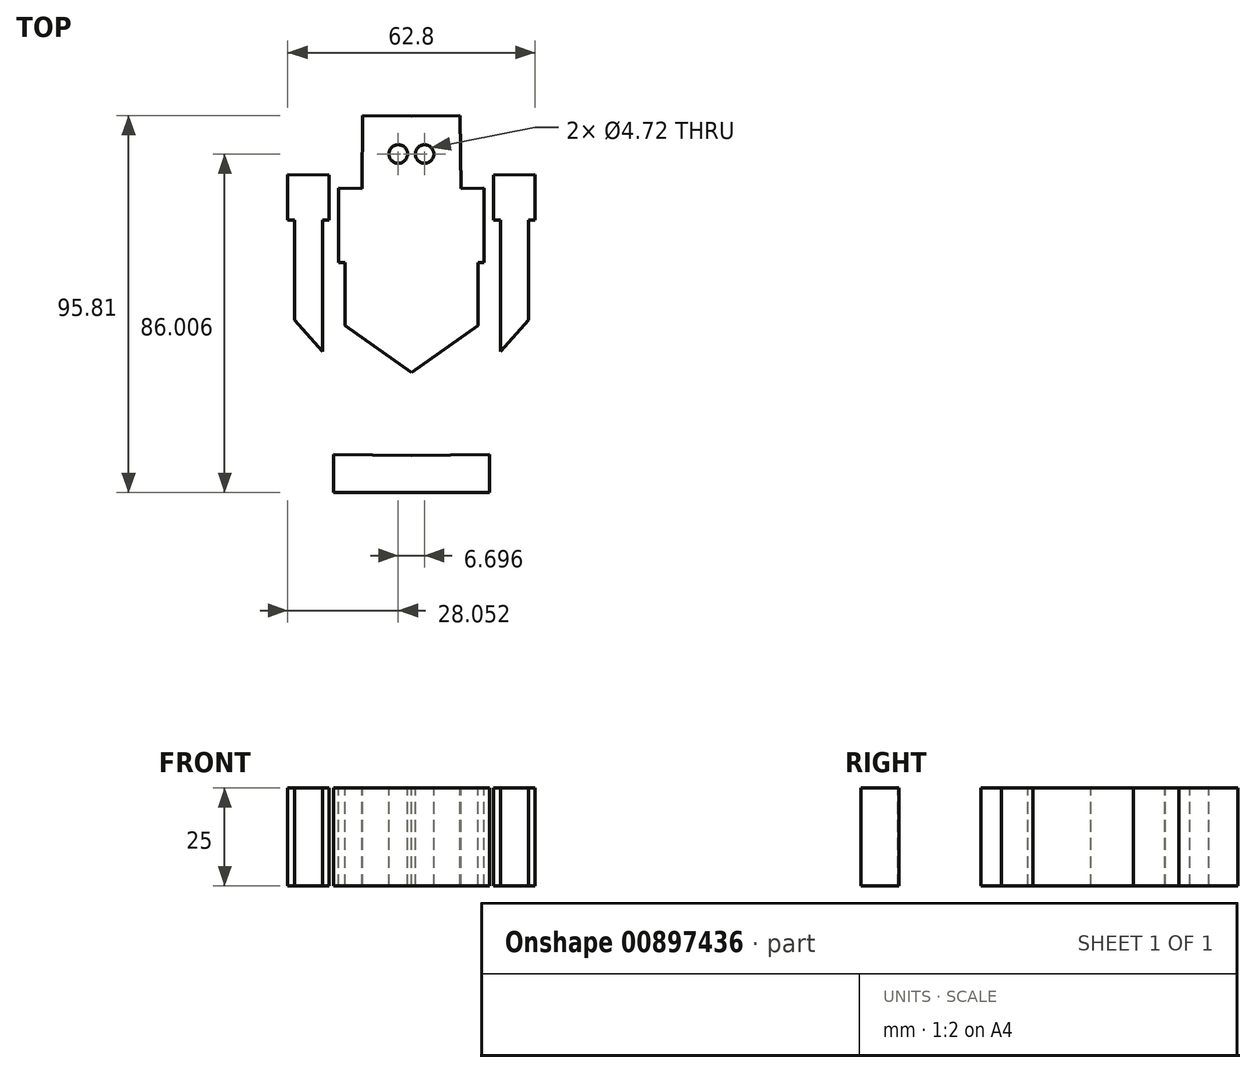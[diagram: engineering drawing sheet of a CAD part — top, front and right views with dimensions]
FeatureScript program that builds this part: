
annotation { "Feature Type Name" : "Feature", "Feature Type Description" : "" }
export const myFeature = defineFeature(function(context is Context, id is Id, definition is map)
    precondition{}
    {
        {
            var Q0;
            Q0=qCreatedBy(makeId("Top.planeOp"),FACE);
            var sketch = newSketch(context, id + "F0", { "sketchPlane" : qUnion([Q0])});
            skLineSegment(sketch, "E0", {"start": v(-49.7, 0) * mm, "end": v(50.3, 0) * mm});
            skLineSegment(sketch, "E1", {"start": v(0, 0) * mm, "end": v(0, 100) * mm});
            skSolve(sketch);
        }
        {
            var Q0;
            Q0=qCreatedBy(makeId("Top.planeOp"),FACE);
            var sketch = newSketch(context, id + "F1", { "sketchPlane" : qUnion([Q0])});
            skLineSegment(sketch, "E2", {"start": v(-31.4, 22.3) * mm, "end": v(-31.4, 10.7) * mm});
            skLineSegment(sketch, "E3", {"start": v(-31.4, 10.7) * mm, "end": v(-20.92, 10.7) * mm});
            skLineSegment(sketch, "E4", {"start": v(-20.92, 10.7) * mm, "end": v(-20.92, 22.18) * mm});
            skLineSegment(sketch, "E5", {"start": v(-20.92, 22.18) * mm, "end": v(-31.4, 22.3) * mm});
            skLineSegment(sketch, "E6", {"start": v(-29.73, 10.7) * mm, "end": v(-29.73, -14.7) * mm});
            skLineSegment(sketch, "E7", {"start": v(-29.73, -14.7) * mm, "end": v(-22.6, -14.78) * mm});
            skLineSegment(sketch, "E8", {"start": v(-22.6, -14.78) * mm, "end": v(-22.6, 10.7) * mm});
            skLineSegment(sketch, "E9", {"start": v(-22.6, -14.78) * mm, "end": v(-22.6, -22.7) * mm});
            skLineSegment(sketch, "E10", {"start": v(-22.6, -22.7) * mm, "end": v(-29.73, -14.7) * mm});
            skLineSegment(sketch, "E11", {"start": v(-19.8, -58.48) * mm, "end": v(-19.8, -48.82) * mm});
            skLineSegment(sketch, "E12", {"start": v(-19.8, -48.82) * mm, "end": v(0, -49.03) * mm});
            skLineSegment(sketch, "E13", {"start": v(-12.9, -48.9) * mm, "end": v(-12.59, -19.79) * mm});
            skLineSegment(sketch, "E14", {"start": v(0, -28.01) * mm, "end": v(-16.87, -16.08) * mm});
            skLineSegment(sketch, "E15", {"start": v(-16.87, -16.08) * mm, "end": v(-16.87, 0) * mm});
            skLineSegment(sketch, "E16", {"start": v(-16.87, -16.08) * mm, "end": v(0, -16.26) * mm});
            skLineSegment(sketch, "E17", {"start": v(0, 18.65) * mm, "end": v(-18.45, 18.84) * mm});
            skLineSegment(sketch, "E18", {"start": v(-18.45, 18.84) * mm, "end": v(-18.45, 0) * mm});
            skLineSegment(sketch, "E19", {"start": v(-18.45, 0) * mm, "end": v(0, 0) * mm});
            skLineSegment(sketch, "E20", {"start": v(0, 0) * mm, "end": v(0, 18.65) * mm});
            skLineSegment(sketch, "E21", {"start": v(-12.59, 18.65) * mm, "end": v(-12.4, 37.33) * mm});
            skLineSegment(sketch, "E22", {"start": v(-12.4, 37.33) * mm, "end": v(0, 37.2) * mm});
            skCircle(sketch, "E23", {"center": v(-3.35, 27.53) * mm, "radius": 2.36 * mm});
            skLineSegment(sketch, "E24.MirrorCS", {"start": v(12.4, 37.33) * mm, "end": v(0, 37.2) * mm});
            skLineSegment(sketch, "E25.MirrorCS", {"start": v(12.59, 18.65) * mm, "end": v(12.4, 37.33) * mm});
            skCircle(sketch, "E26.MirrorC", {"center": v(3.35, 27.53) * mm, "radius": 2.36 * mm});
            skLineSegment(sketch, "E27.MirrorCS", {"start": v(0, 18.65) * mm, "end": v(18.45, 18.84) * mm});
            skLineSegment(sketch, "E28.MirrorCS", {"start": v(18.45, 18.84) * mm, "end": v(18.45, 0) * mm});
            skLineSegment(sketch, "E29.MirrorCS", {"start": v(18.45, 0) * mm, "end": v(0, 0) * mm});
            skLineSegment(sketch, "E30.MirrorCS", {"start": v(16.87, -16.08) * mm, "end": v(16.87, 0) * mm});
            skLineSegment(sketch, "E31.MirrorCS", {"start": v(16.87, -16.08) * mm, "end": v(0, -16.26) * mm});
            skLineSegment(sketch, "E32.MirrorCS", {"start": v(0, -28.01) * mm, "end": v(16.87, -16.08) * mm});
            skLineSegment(sketch, "E33.MirrorCS", {"start": v(12.9, -48.9) * mm, "end": v(12.59, -19.79) * mm});
            skLineSegment(sketch, "E34.MirrorCS", {"start": v(19.8, -48.82) * mm, "end": v(0, -49.03) * mm});
            skLineSegment(sketch, "E35.MirrorCS", {"start": v(19.8, -58.48) * mm, "end": v(19.8, -48.82) * mm});
            skLineSegment(sketch, "E36.MirrorCS", {"start": v(20.92, 22.18) * mm, "end": v(31.4, 22.3) * mm});
            skLineSegment(sketch, "E37.MirrorCS", {"start": v(31.4, 22.3) * mm, "end": v(31.4, 10.7) * mm});
            skLineSegment(sketch, "E38.MirrorCS", {"start": v(20.92, 10.7) * mm, "end": v(20.92, 22.18) * mm});
            skLineSegment(sketch, "E39.MirrorCS", {"start": v(31.4, 10.7) * mm, "end": v(20.92, 10.7) * mm});
            skLineSegment(sketch, "E40.MirrorCS", {"start": v(29.73, 10.7) * mm, "end": v(29.73, -14.7) * mm});
            skLineSegment(sketch, "E41.MirrorCS", {"start": v(22.6, -14.78) * mm, "end": v(22.6, 10.7) * mm});
            skLineSegment(sketch, "E42.MirrorCS", {"start": v(29.73, -14.7) * mm, "end": v(22.6, -14.78) * mm});
            skLineSegment(sketch, "E43.MirrorCS", {"start": v(22.6, -22.7) * mm, "end": v(29.73, -14.7) * mm});
            skLineSegment(sketch, "E44.MirrorCS", {"start": v(22.6, -14.78) * mm, "end": v(22.6, -22.7) * mm});
            skLineSegment(sketch, "E45", {"start": v(19.8, -58.48) * mm, "end": v(-19.8, -58.48) * mm});
            skLineSegment(sketch, "E46", {"start": v(0, -28.01) * mm, "end": v(0, -49.03) * mm});
            skSolve(sketch);
        }
        {
            var Q0;
            Q0 = qSketchRegion(id + "F1", true);
            extrude(context, id + "F2", {"entities" : qUnion([Q0]), "oppositeDirection" : true, "depth" : 25 * mm, "offsetDistance" : 25 * mm});
        }
    });
